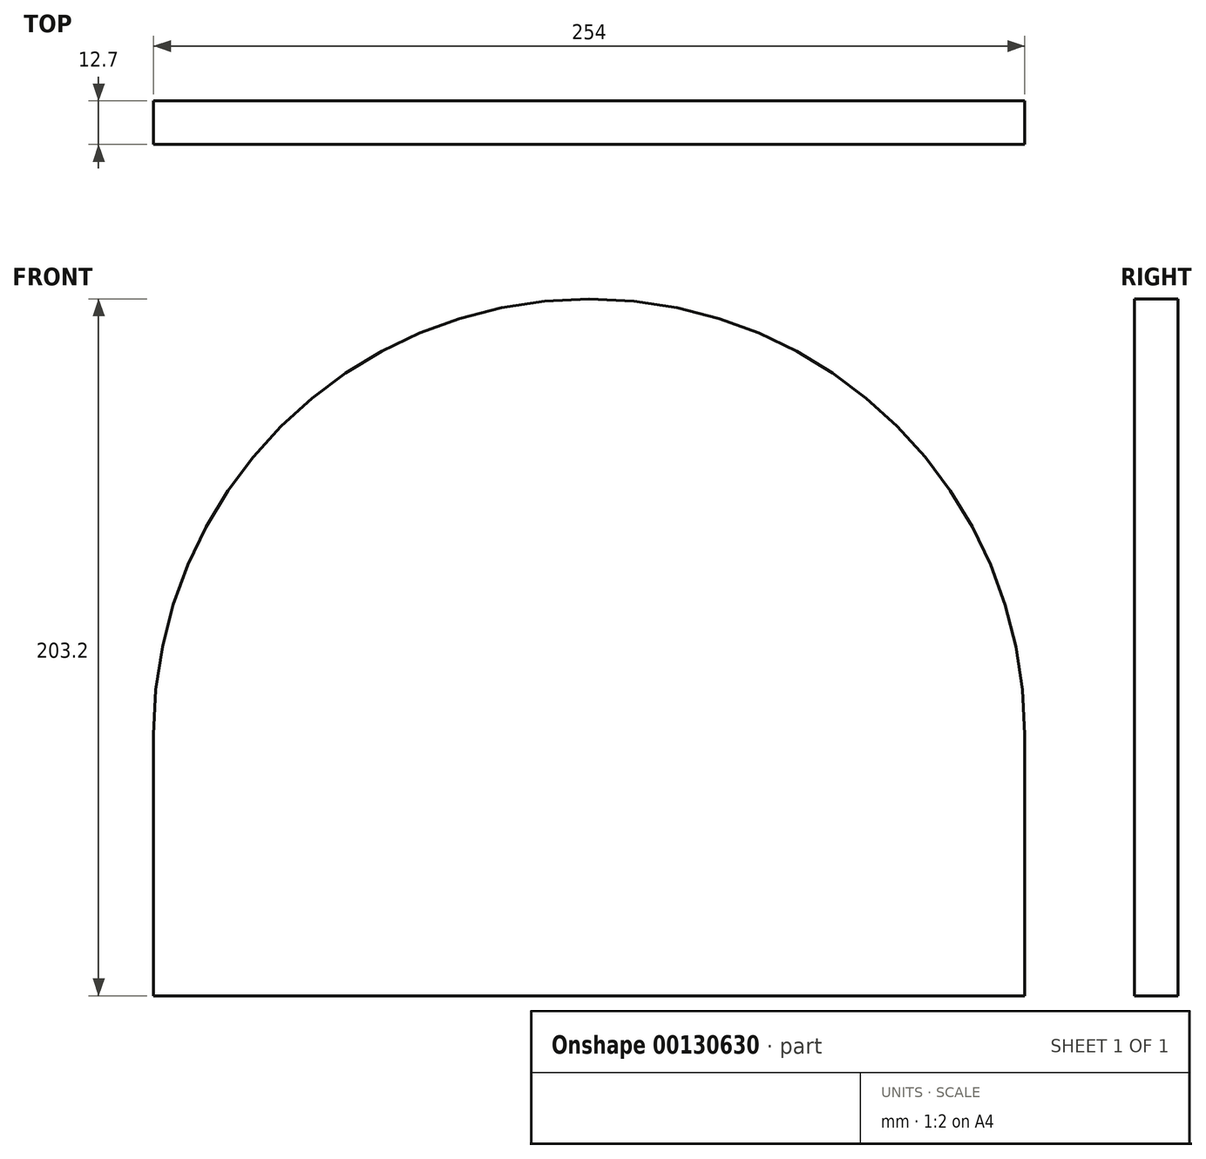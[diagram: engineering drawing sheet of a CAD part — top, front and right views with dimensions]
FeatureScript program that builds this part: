
annotation { "Feature Type Name" : "Feature", "Feature Type Description" : "" }
export const myFeature = defineFeature(function(context is Context, id is Id, definition is map)
    precondition{}
    {
        {
            var Q0;
            Q0=qCreatedBy(makeId("Front.planeOp"),FACE);
            var sketch = newSketch(context, id + "F0", { "sketchPlane" : qUnion([Q0])});
            skLineSegment(sketch, "E0.bottom", {"start": v(-114.6, 0) * mm, "end": v(139.4, 0) * mm});
            skLineSegment(sketch, "E0.top", {"start": v(12.4, 203.2) * mm, "end": v(12.4, 203.2) * mm});
            skLineSegment(sketch, "E0.left", {"start": v(-114.6, 0) * mm, "end": v(-114.6, 76.2) * mm});
            skLineSegment(sketch, "E0.right", {"start": v(139.4, 0) * mm, "end": v(139.4, 76.2) * mm});
            skPoint(sketch, "E1.visualSharp", {"position": v(-114.6, 203.2) * mm});
            skArc(sketch, "E1.filletArc", {"start": v(12.4, 203.2) * mm, "mid": v(-77.4, 166) * mm, "end": v(-114.6, 76.2) * mm});
            skPoint(sketch, "E2.visualSharp", {"position": v(139.4, 203.2) * mm});
            skArc(sketch, "E2.filletArc", {"start": v(139.4, 76.2) * mm, "mid": v(102.2, 166) * mm, "end": v(12.4, 203.2) * mm});
            skSolve(sketch);
        }
        {
            var Q0;
            Q0=makeQuery(id+"F0.imprint","IMPRINT",FACE,{"disambiguationData":[TD([[makeQuery(id+"F0.imprint","IMPRINT",EDGE,{"derivedFrom":sQuery(id+"F0.wireOp",EDGE,"E0.bottom")}),1.0]])]});
            extrude(context, id + "F1", {"entities" : qUnion([Q0]), "depth" : 12.7 * mm});
        }
    });
